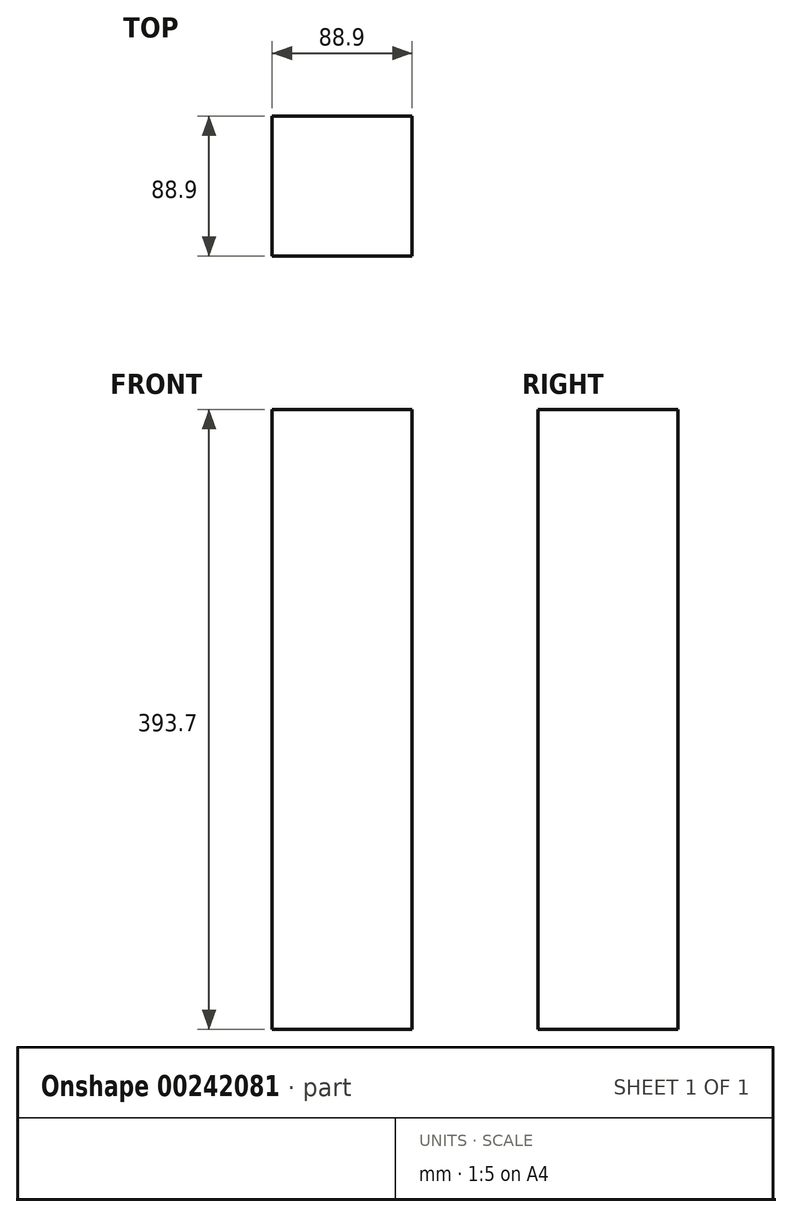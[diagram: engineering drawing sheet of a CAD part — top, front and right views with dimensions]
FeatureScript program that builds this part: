
annotation { "Feature Type Name" : "Feature", "Feature Type Description" : "" }
export const myFeature = defineFeature(function(context is Context, id is Id, definition is map)
    precondition{}
    {
        {
            var Q0;
            Q0=qCreatedBy(makeId("Top.planeOp"),FACE);
            var sketch = newSketch(context, id + "F0", { "sketchPlane" : qUnion([Q0])});
            skLineSegment(sketch, "E0.bottom", {"start": v(-88.9, 88.9) * mm, "end": v(0, 88.9) * mm});
            skLineSegment(sketch, "E0.top", {"start": v(-88.9, 0) * mm, "end": v(0, 0) * mm});
            skLineSegment(sketch, "E0.left", {"start": v(-88.9, 88.9) * mm, "end": v(-88.9, 0) * mm});
            skLineSegment(sketch, "E0.right", {"start": v(0, 88.9) * mm, "end": v(0, 0) * mm});
            skSolve(sketch);
        }
        {
            var Q0;
            Q0=makeQuery(id+"F0.imprint","IMPRINT",FACE,{"disambiguationData":[TD([[makeQuery(id+"F0.imprint","IMPRINT",EDGE,{"derivedFrom":sQuery(id+"F0.wireOp",EDGE,"E0.bottom")}),-1.0]])]});
            extrude(context, id + "F1", {"entities" : qUnion([Q0]), "depth" : 393.7 * mm});
        }
    });
